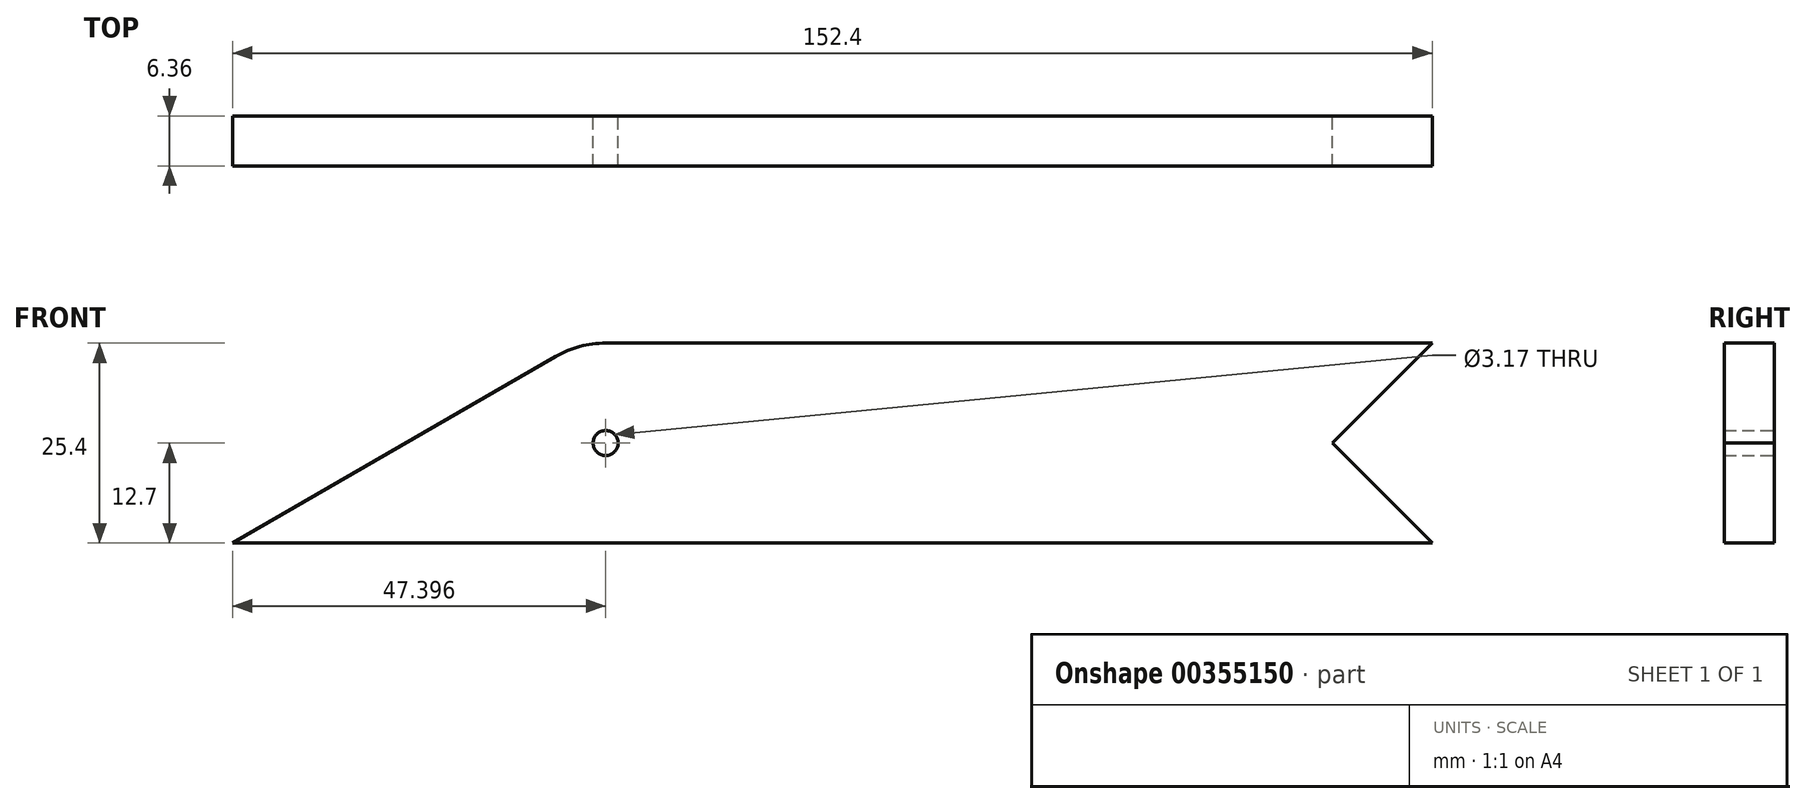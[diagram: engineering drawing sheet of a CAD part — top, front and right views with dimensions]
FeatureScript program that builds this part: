
annotation { "Feature Type Name" : "Feature", "Feature Type Description" : "" }
export const myFeature = defineFeature(function(context is Context, id is Id, definition is map)
    precondition{}
    {
        {
            var Q0;
            Q0=qCreatedBy(makeId("Front.planeOp"),FACE);
            var sketch = newSketch(context, id + "F0", { "sketchPlane" : qUnion([Q0])});
            skLineSegment(sketch, "E0", {"start": v(87.99, -152.4) * mm, "end": v(-263.96, -152.4) * mm});
            skLineSegment(sketch, "E1", {"start": v(-263.96, -152.4) * mm, "end": v(0, 0) * mm});
            skLineSegment(sketch, "E2", {"start": v(0, 0) * mm, "end": v(87.99, -152.4) * mm});
            skLineSegment(sketch, "E3", {"start": v(0, 0) * mm, "end": v(152.4, 87.99) * mm, "construction": true});
            skLineSegment(sketch, "E4", {"start": v(152.4, 87.99) * mm, "end": v(87.99, -152.4) * mm, "construction": true});
            skCircle(sketch, "E5", {"center": v(0, 0) * mm, "radius": 9.53 * mm});
            skCircle(sketch, "E6", {"center": v(0, 0) * mm, "radius": 12.7 * mm});
            skCircle(sketch, "E7", {"center": v(-263.96, -152.4) * mm, "radius": 12.7 * mm});
            skCircle(sketch, "E8", {"center": v(87.99, -152.4) * mm, "radius": 12.7 * mm});
            skLineSegment(sketch, "E9", {"start": v(-6.35, 11) * mm, "end": v(-270.31, -141.4) * mm});
            skLineSegment(sketch, "E10", {"start": v(-263.96, -165.1) * mm, "end": v(87.99, -165.1) * mm});
            skLineSegment(sketch, "E11", {"start": v(98.99, -146.05) * mm, "end": v(11, 6.35) * mm});
            skLineSegment(sketch, "E12", {"start": v(76.99, -158.75) * mm, "end": v(-11, -6.35) * mm});
            skLineSegment(sketch, "E13", {"start": v(-257.61, -163.4) * mm, "end": v(6.35, -11) * mm});
            skLineSegment(sketch, "E14", {"start": v(87.99, -139.7) * mm, "end": v(-263.96, -139.7) * mm});
            skLineSegment(sketch, "E15", {"start": v(87.99, -165.1) * mm, "end": v(109.99, -165.1) * mm});
            skLineSegment(sketch, "E16", {"start": v(98.99, -146.05) * mm, "end": v(109.99, -165.1) * mm});
            skCircle(sketch, "E17", {"center": v(87.99, -152.4) * mm, "radius": 1.59 * mm});
            skCircle(sketch, "E18", {"center": v(-263.96, -152.4) * mm, "radius": 1.59 * mm});
            skLineSegment(sketch, "E19", {"start": v(-270.31, -141.4) * mm, "end": v(-311.36, -165.1) * mm});
            skLineSegment(sketch, "E20", {"start": v(-263.96, -165.1) * mm, "end": v(-311.36, -165.1) * mm});
            skLineSegment(sketch, "E21", {"start": v(-77.11, -139.7) * mm, "end": v(-89.81, -152.4) * mm});
            skLineSegment(sketch, "E22", {"start": v(-89.81, -152.4) * mm, "end": v(-77.11, -165.1) * mm});
            skLineSegment(sketch, "E23", {"start": v(-77.11, -139.7) * mm, "end": v(-77.11, -165.1) * mm});
            skLineSegment(sketch, "E24", {"start": v(-158.96, -139.7) * mm, "end": v(-171.66, -152.4) * mm});
            skLineSegment(sketch, "E25", {"start": v(-171.66, -152.4) * mm, "end": v(-158.96, -165.1) * mm});
            skLineSegment(sketch, "E26", {"start": v(-158.96, -139.7) * mm, "end": v(-158.96, -165.1) * mm});
            skSolve(sketch);
        }
        {
            var Q0;
            {var subQ0=sQuery(id+"F0.wireOp",EDGE,"E19");Q0=makeQuery(id+"F0.imprint","IMPRINT",FACE,{"disambiguationData":[TD([[makeQuery(id+"F0.imprint","IMPRINT",EDGE,{"derivedFrom":subQ0}),1.0]])]});}
            var Q1;
            {var subQ0=sQuery(id+"F0.wireOp",EDGE,"E7");var subQ3=sQuery(id+"F0.wireOp",EDGE,"E0");var subQ4=makeQuery(id+"F0.imprint","INTERSECT",VERTEX,{"derivedFrom":[subQ3,subQ0]});Q1=makeQuery(id+"F0.imprint","IMPRINT",FACE,{"disambiguationData":[TD([[makeQuery(id+"F0.imprint","IMPRINT",EDGE,{"disambiguationData":[TD([[subQ4,-1.0]])],"derivedFrom":subQ3}),1.0]])]});}
            var Q2;
            {var subQ0=sQuery(id+"F0.wireOp",EDGE,"E7");var subQ1=sQuery(id+"F0.wireOp",EDGE,"E0");var subQ2=makeQuery(id+"F0.imprint","INTERSECT",VERTEX,{"derivedFrom":[subQ1,subQ0]});Q2=makeQuery(id+"F0.imprint","IMPRINT",FACE,{"disambiguationData":[TD([[makeQuery(id+"F0.imprint","IMPRINT",EDGE,{"disambiguationData":[TD([[subQ2,-1.0]])],"derivedFrom":subQ1}),-1.0]])]});}
            var Q3;
            {var subQ0=sQuery(id+"F0.wireOp",EDGE,"E13");var subQ1=sQuery(id+"F0.wireOp",EDGE,"E0");var subQ2=makeQuery(id+"F0.imprint","INTERSECT",VERTEX,{"derivedFrom":[subQ1,subQ0]});Q3=makeQuery(id+"F0.imprint","IMPRINT",FACE,{"disambiguationData":[TD([[makeQuery(id+"F0.imprint","IMPRINT",EDGE,{"disambiguationData":[TD([[subQ2,-1.0]])],"derivedFrom":subQ1}),1.0]])]});}
            var Q4;
            {var subQ0=sQuery(id+"F0.wireOp",EDGE,"E7");var subQ1=sQuery(id+"F0.wireOp",EDGE,"E1");var subQ2=makeQuery(id+"F0.imprint","INTERSECT",VERTEX,{"derivedFrom":[subQ1,subQ0]});Q4=makeQuery(id+"F0.imprint","IMPRINT",FACE,{"disambiguationData":[TD([[makeQuery(id+"F0.imprint","IMPRINT",EDGE,{"disambiguationData":[TD([[subQ2,-1.0]])],"derivedFrom":subQ1}),1.0]])]});}
            var Q5;
            {var subQ0=sQuery(id+"F0.wireOp",EDGE,"E13");var subQ1=sQuery(id+"F0.wireOp",EDGE,"E0");var subQ2=makeQuery(id+"F0.imprint","INTERSECT",VERTEX,{"derivedFrom":[subQ1,subQ0]});Q5=makeQuery(id+"F0.imprint","IMPRINT",FACE,{"disambiguationData":[TD([[makeQuery(id+"F0.imprint","IMPRINT",EDGE,{"disambiguationData":[TD([[subQ2,-1.0]])],"derivedFrom":subQ1}),-1.0]])]});}
            var Q6;
            {var subQ0=sQuery(id+"F0.wireOp",EDGE,"E24");Q6=makeQuery(id+"F0.imprint","IMPRINT",FACE,{"disambiguationData":[TD([[makeQuery(id+"F0.imprint","IMPRINT",EDGE,{"derivedFrom":subQ0}),-1.0]])]});}
            var Q7;
            {var subQ7=sQuery(id+"F0.wireOp",EDGE,"E25");Q7=makeQuery(id+"F0.imprint","IMPRINT",FACE,{"disambiguationData":[TD([[makeQuery(id+"F0.imprint","IMPRINT",EDGE,{"derivedFrom":subQ7}),-1.0]])]});}
            extrude(context, id + "F1", {"entities" : qUnion([Q0, Q1, Q2, Q3, Q4, Q5, Q6, Q7]), "endBound" : BoundingType.SYMMETRIC, "depth" : 6.35 * mm});
        }
    });
